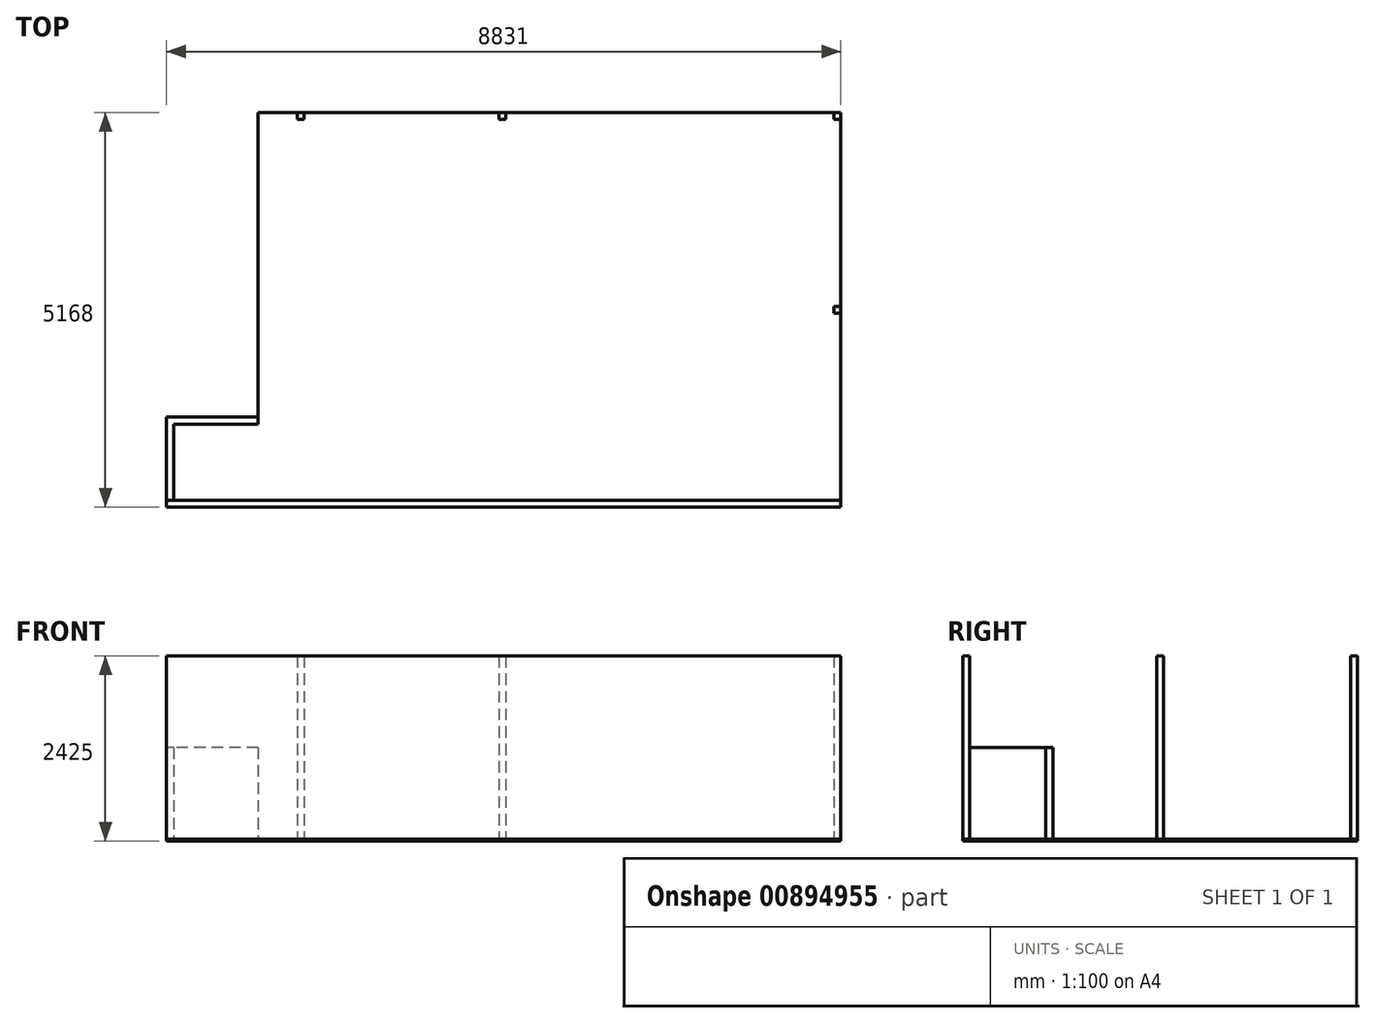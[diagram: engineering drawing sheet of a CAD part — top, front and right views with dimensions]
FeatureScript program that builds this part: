
annotation { "Feature Type Name" : "Feature", "Feature Type Description" : "" }
export const myFeature = defineFeature(function(context is Context, id is Id, definition is map)
    precondition{}
    {
        {
            var Q0;
            Q0=qCreatedBy(makeId("Top.planeOp"),FACE);
            var sketch = newSketch(context, id + "F0", { "sketchPlane" : qUnion([Q0])});
            skLineSegment(sketch, "E0.bottom", {"start": v(0, 2447) * mm, "end": v(-90, 2447) * mm});
            skLineSegment(sketch, "E0.top", {"start": v(0, 2537) * mm, "end": v(-90, 2537) * mm});
            skLineSegment(sketch, "E0.left", {"start": v(0, 2447) * mm, "end": v(0, 2537) * mm});
            skLineSegment(sketch, "E0.right", {"start": v(-90, 2447) * mm, "end": v(-90, 2537) * mm});
            skLineSegment(sketch, "E1.bottom", {"start": v(0, 4988) * mm, "end": v(-90, 4988) * mm});
            skLineSegment(sketch, "E1.top", {"start": v(0, 5078) * mm, "end": v(-90, 5078) * mm});
            skLineSegment(sketch, "E1.left", {"start": v(0, 4988) * mm, "end": v(0, 5078) * mm});
            skLineSegment(sketch, "E1.right", {"start": v(-90, 4988) * mm, "end": v(-90, 5078) * mm});
            skLineSegment(sketch, "E2.bottom", {"start": v(-4386, 5078) * mm, "end": v(-4476, 5078) * mm});
            skLineSegment(sketch, "E2.top", {"start": v(-4386, 4988) * mm, "end": v(-4476, 4988) * mm});
            skLineSegment(sketch, "E2.left", {"start": v(-4386, 5078) * mm, "end": v(-4386, 4988) * mm});
            skLineSegment(sketch, "E2.right", {"start": v(-4476, 5078) * mm, "end": v(-4476, 4988) * mm});
            skLineSegment(sketch, "E3.bottom", {"start": v(-7031, 5078) * mm, "end": v(-7121, 5078) * mm});
            skLineSegment(sketch, "E3.top", {"start": v(-7031, 4988) * mm, "end": v(-7121, 4988) * mm});
            skLineSegment(sketch, "E3.left", {"start": v(-7031, 5078) * mm, "end": v(-7031, 4988) * mm});
            skLineSegment(sketch, "E3.right", {"start": v(-7121, 5078) * mm, "end": v(-7121, 4988) * mm});
            skLineSegment(sketch, "E4", {"start": v(-7121, 5078) * mm, "end": v(-7631, 5078) * mm, "construction": true});
            skLineSegment(sketch, "E5", {"start": v(-7631, 5078) * mm, "end": v(-7631, 998) * mm, "construction": true});
            skLineSegment(sketch, "E6.bottom", {"start": v(-7631, 998) * mm, "end": v(-8741, 998) * mm});
            skLineSegment(sketch, "E6.top", {"start": v(-7631, 1088) * mm, "end": v(-8831, 1088) * mm});
            skLineSegment(sketch, "E6.left", {"start": v(-7631, 998) * mm, "end": v(-7631, 1088) * mm});
            skLineSegment(sketch, "E6.right", {"start": v(-8831, 998) * mm, "end": v(-8831, 1088) * mm});
            skLineSegment(sketch, "E7", {"start": v(-7121, 5078) * mm, "end": v(-7631, 5078) * mm});
            skLineSegment(sketch, "E8", {"start": v(-7631, 5078) * mm, "end": v(-7631, 1088) * mm});
            skLineSegment(sketch, "E9", {"start": v(-7031, 5078) * mm, "end": v(0, 5078) * mm});
            skLineSegment(sketch, "E10", {"start": v(0, 5078) * mm, "end": v(0, 0) * mm});
            skLineSegment(sketch, "E11", {"start": v(0, 0) * mm, "end": v(-8831, 0) * mm});
            skLineSegment(sketch, "E12", {"start": v(-8831, 0) * mm, "end": v(-8831, 998) * mm});
            skLineSegment(sketch, "E13.0", {"start": v(-8741, 0) * mm, "end": v(-8741, 998) * mm});
            skLineSegment(sketch, "E14.0", {"start": v(0, -90) * mm, "end": v(-8831, -90) * mm});
            skLineSegment(sketch, "E15", {"start": v(-8831, 0) * mm, "end": v(-8831, -90) * mm});
            skLineSegment(sketch, "E16", {"start": v(0, 0) * mm, "end": v(0, -90) * mm});
            skLineSegment(sketch, "E17", {"start": v(-7121, 5033) * mm, "end": v(-7731.54, 5033) * mm, "construction": true});
            skLineSegment(sketch, "E18.0", {"start": v(-7586, 5078) * mm, "end": v(-7586, 998) * mm, "construction": true});
            skLineSegment(sketch, "E19", {"start": v(-7631, 1043) * mm, "end": v(-7510.25, 1043) * mm, "construction": true});
            skSolve(sketch);
        }
        {
            var Q0;
            Q0=makeQuery(id+"F0.imprint","IMPRINT",FACE,{"disambiguationData":[TD([[makeQuery(id+"F0.imprint","IMPRINT",EDGE,{"derivedFrom":sQuery(id+"F0.wireOp",EDGE,"E6.bottom")}),-1.0]])]});
            extrude(context, id + "F1", {"entities" : qUnion([Q0]), "depth" : 1200 * mm, "offsetDistance" : 25 * mm});
        }
        {
            var Q0;
            Q0=makeQuery(id+"F0.imprint","IMPRINT",FACE,{"disambiguationData":[TD([[makeQuery(id+"F0.imprint","IMPRINT",EDGE,{"derivedFrom":sQuery(id+"F0.wireOp",EDGE,"E14.0")}),-1.0]])]});
            extrude(context, id + "F2", {"entities" : qUnion([Q0]), "operationType" : NewBodyOperationType.ADD, "depth" : 2400 * mm, "offsetDistance" : 25 * mm});
        }
        {
            var Q0;
            {var subQ0=sQuery(id+"F0.wireOp",EDGE,"E0.bottom");Q0=makeQuery(id+"F0.imprint","IMPRINT",FACE,{"disambiguationData":[TD([[makeQuery(id+"F0.imprint","IMPRINT",EDGE,{"derivedFrom":subQ0}),-1.0]])]});}
            var Q1;
            {var subQ0=sQuery(id+"F0.wireOp",EDGE,"E1.bottom");Q1=makeQuery(id+"F0.imprint","IMPRINT",FACE,{"disambiguationData":[TD([[makeQuery(id+"F0.imprint","IMPRINT",EDGE,{"derivedFrom":subQ0}),-1.0]])]});}
            var Q2;
            Q2=makeQuery(id+"F0.imprint","IMPRINT",FACE,{"disambiguationData":[TD([[makeQuery(id+"F0.imprint","IMPRINT",EDGE,{"derivedFrom":sQuery(id+"F0.wireOp",EDGE,"E2.top")}),-1.0]])]});
            var Q3;
            Q3=makeQuery(id+"F0.imprint","IMPRINT",FACE,{"disambiguationData":[TD([[makeQuery(id+"F0.imprint","IMPRINT",EDGE,{"derivedFrom":sQuery(id+"F0.wireOp",EDGE,"E3.bottom")}),1.0]])]});
            extrude(context, id + "F3", {"entities" : qUnion([Q0, Q1, Q2, Q3]), "depth" : 2400 * mm, "offsetDistance" : 25 * mm});
        }
        {
            var Q0;
            {var subQ5=sQuery(id+"F0.wireOp",EDGE,"E0.bottom");Q0=makeQuery(id+"F0.imprint","IMPRINT",FACE,{"disambiguationData":[TD([[makeQuery(id+"F0.imprint","IMPRINT",EDGE,{"derivedFrom":subQ5}),1.0]])]});}
            var Q1;
            Q1=makeQuery(id+"F0.imprint","IMPRINT",FACE,{"disambiguationData":[TD([[makeQuery(id+"F0.imprint","IMPRINT",EDGE,{"derivedFrom":sQuery(id+"F0.wireOp",EDGE,"E14.0")}),-1.0]])]});
            var Q2;
            Q2=makeQuery(id+"F0.imprint","IMPRINT",FACE,{"disambiguationData":[TD([[makeQuery(id+"F0.imprint","IMPRINT",EDGE,{"derivedFrom":sQuery(id+"F0.wireOp",EDGE,"E6.bottom")}),-1.0]])]});
            var Q3;
            Q3=makeQuery(id+"F0.imprint","IMPRINT",FACE,{"disambiguationData":[TD([[makeQuery(id+"F0.imprint","IMPRINT",EDGE,{"derivedFrom":sQuery(id+"F0.wireOp",EDGE,"E3.bottom")}),1.0]])]});
            var Q4;
            Q4=makeQuery(id+"F0.imprint","IMPRINT",FACE,{"disambiguationData":[TD([[makeQuery(id+"F0.imprint","IMPRINT",EDGE,{"derivedFrom":sQuery(id+"F0.wireOp",EDGE,"E2.top")}),-1.0]])]});
            var Q5;
            {var subQ0=sQuery(id+"F0.wireOp",EDGE,"E1.bottom");Q5=makeQuery(id+"F0.imprint","IMPRINT",FACE,{"disambiguationData":[TD([[makeQuery(id+"F0.imprint","IMPRINT",EDGE,{"derivedFrom":subQ0}),-1.0]])]});}
            var Q6;
            {var subQ0=sQuery(id+"F0.wireOp",EDGE,"E0.bottom");Q6=makeQuery(id+"F0.imprint","IMPRINT",FACE,{"disambiguationData":[TD([[makeQuery(id+"F0.imprint","IMPRINT",EDGE,{"derivedFrom":subQ0}),-1.0]])]});}
            extrude(context, id + "F4", {"entities" : qUnion([Q0, Q1, Q2, Q3, Q4, Q5, Q6]), "oppositeDirection" : true, "depth" : 25 * mm, "offsetDistance" : 25 * mm});
        }
    });
